# Revit family: Gira_216200
name_source: partatom
category: Electrical Fixtures
revit_build: Autodesk Revit 2017 (Build: 20160225_1515(x64)
units: mm (PartAtom-declared; Revit-internal decimal feet)

## family parameters
Cut with Voids When Loaded = No
Host = Face
Maintain Annotation Orientation = No
Part Type = Normal
Room Calculation Point = No
Round Connector Dimension = Use Diameter
Shared = No

## types (1)
- Room act. KNX DRA
    BIM = https://media.live.bim.site 8f.rfa
    BIMSITE_PRODUCT_ID = a7ec78d93201e89a0426071e1eb0df07dd7cfba7
    Bus connection included = No
    Cost = 0 $
    Default Elevation = 1219 mm
    Description = Room act.DRA KNX KNX room actuator,DRA plus Features: - The room actuator controls three functions simultaneously in one device, such as lighting, blind and heating. The four relay outputs can be set either for blind operation or alternatively for switching operation in the ETS (Engineering Tool Software). Mixed operation is also possible. - Two switching outputs make one blind output. - In addition, there are two further electronic switching outputs for the control of servos. Switching operation: - The room actuator with its relay contacts controls electrical devices such as lighting systems. The relay contacts have flip-flop contacts, so that the last set switching condition remains unchanged even if the power supply fails. - Functional properties for each output: a wide spectrum of time functions, logical links, scenes, block functions or restraints, extended feedback, cyclical monitoring of incoming switching telegrams and an elapsed operating time meter. Blind operation: - The room actuator uses its relay contacts to control electrically operated blinds, shutters, awnings, ventilation flaps,or similar hangings with a mains voltage of AC 230 V. - Functional properties for each output channel: separately parameterisable movement times, extended feedback functions, assignments of up to 5 various safety functions, a comprehensive solar protection function and the integrating in scenes or restraints. Room temperature control: - Two further electronic switching outputs are used for silent operation of electro thermic servos for heating or cooling systems. - Continuous correcting variable telegrams are implemented in a pulse width modulated output signal (PWM). With this the servos can be continuously controlled. Alternatively, implementing switching correcting variables is also possible. Status message for the valve position and cyclical monitoring of correcting variable telegrams. - Emergency mode in case of bus voltage failure or bus mains voltage recovery plus forced setting via bus telegram for summer and winter mode. - An alarm is triggered in case of short circuit or overload of the switching output and position protection for the valves. De-energised closed or open valve drives can be connected - Monitoring of mains voltage supply, and in cases of malfunction, the transmission of an alarm message on the bus. - Group messages all valves closed" and "largest correcting variable".,Notes : - VDE approval in accordance with EN 60669-1, EN 60669-2-1. - Installation on DIN top-hat rail."
    GTIN = 4010337059370
    HAN = 216200
    Handschaltung = No
    HeinzeBIM = https://www.heinze.de
    LED controlling = No
    Local operation/hand operation = No
    Manufacturer = Gira
    Max. number of venetian-blind outputs = 0
    Max. switching current [Ampere] = 2300
    Number of binary inputs = 0
    Number of inputs = 0
    Number of outputs = 0
    Rated current [Ampere] = 0
    Stellgröße schaltend = No
    Stellgröße stetig = No
    Suitable for C-load = No
    URL = https://www.gira.de
    Ventilschutzfunktion = No
    Verschiedene Phasen anschließbar = No
    With switch function = Yes

## geometry (parser evidence)
native form markers: Blend x2, Sweep x3
no freeform markers — native parametric forms only
